# Revit family: Plum Fix_Toilet Pan_Argent_Pace HygienicFlush BTW_S&P Trap_RearEntry
name_source: partatom
category: Plumbing Fixtures
revit_build: Autodesk Revit 2016 (Build: 20190508_0715(x64)
units: mm (PartAtom-declared; Revit-internal decimal feet)

## family parameters
Always vertical = Yes
Cut with Voids When Loaded = Yes
OmniClass Number = 23.45.05.21.11
OmniClass Title = Water Closets
Part Type = Normal
Room Calculation Point = No
Round Connector Dimension = Use Diameter
Shared = No
Work Plane-Based = No

## types (2) — shared parameters
Angle Offset = 0 mm
Body Material = z_Argent_Ceramic White
BodyMaterial = z_Argent_Ceramic White
CW Connection = Yes
Description = Pace HygienicFlush BTW Toilet S&P Trap with Rear Water Entry
HW Connection = No
IfcExportAs = IfcSanitaryTerminalType
IfcExportType = TOILETPAN
Manufacturer = Argent
Manufacturer_Overall Depth = 630 mm
Manufacturer_Overall Height = 785 mm
Manufacturer_Overall Width = 375 mm
Manufacturer_Spec Code = 807901S4RB
Manufacturer_URL__Product Specific = https://www.argentaust.com.au
Model = 807901S4RB
ModifiedIssue_ANZRS = 20191126 $
Type Comments = S&P Trap
URL = https://www.argentaust.com.au
Uniclass2015Code = Pr_40_20_93_97
Uniclass2015Title = WC suites
Uniclass2015Version = Products v1.5
Vent Connection = No
Waste Connection = Yes
zero-valued in all types: CWFU, Cost, HWFU, WFU

## per-type parameters (varying)
| type | Toilet P Trap | Toilet S Trap | Trap Angle | Trap Offset Value |
| P-Trap | Yes | No | 270.00° | 170 mm |
| S-Trap | No | Yes | 0.00° | 0 mm |

## geometry (parser evidence)
native form markers: Sweep x2
no freeform markers — native parametric forms only
